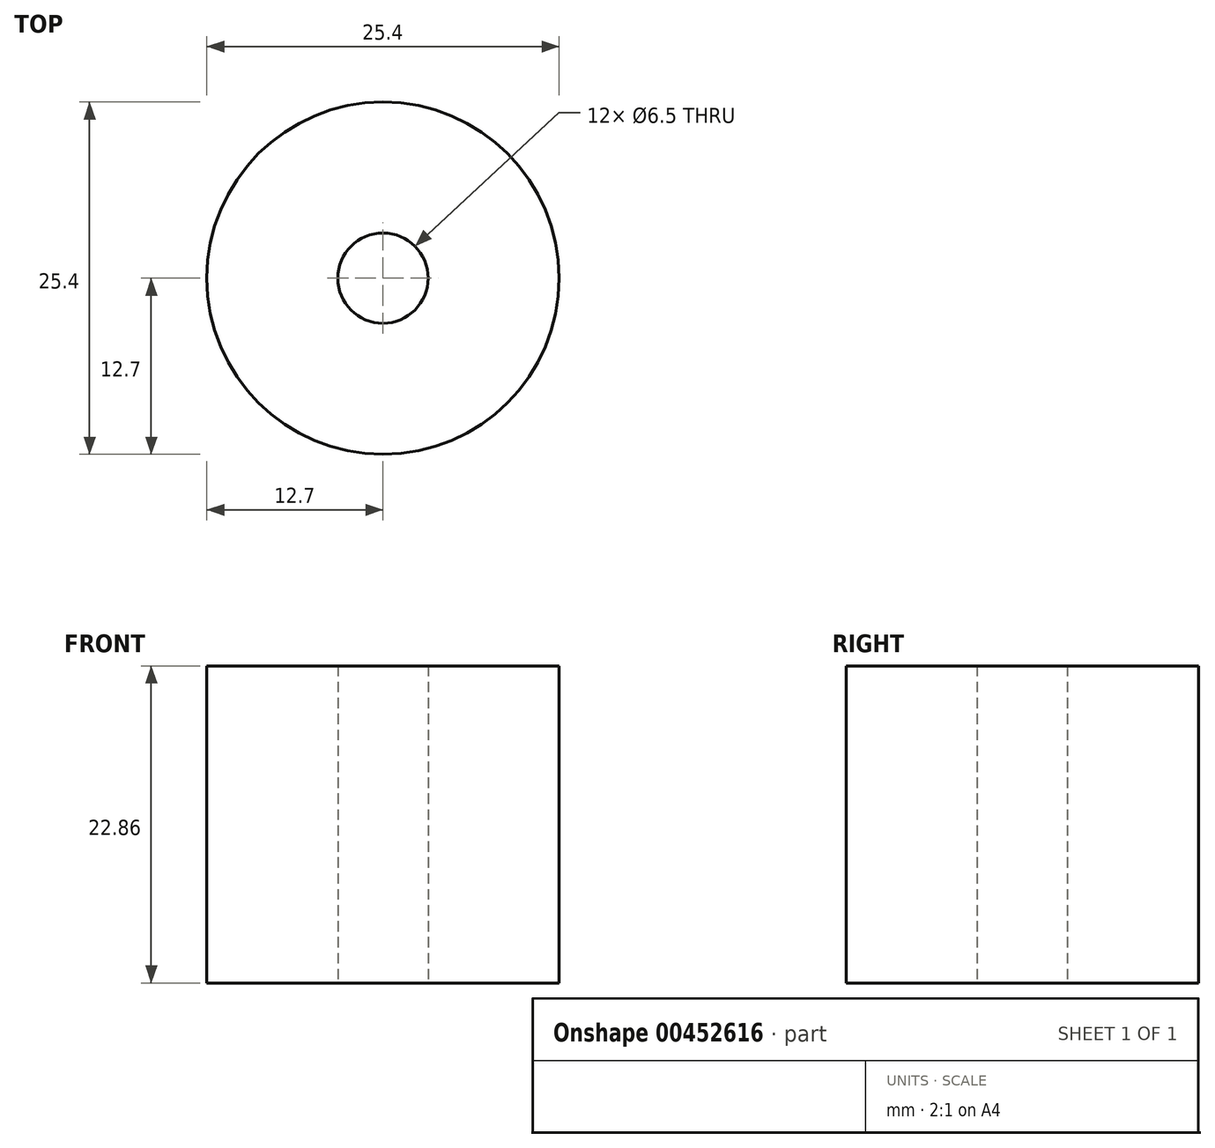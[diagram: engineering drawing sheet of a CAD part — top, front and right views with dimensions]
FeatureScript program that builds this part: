
annotation { "Feature Type Name" : "Feature", "Feature Type Description" : "" }
export const myFeature = defineFeature(function(context is Context, id is Id, definition is map)
    precondition{}
    {
        {
            var Q0;
            Q0=qCreatedBy(makeId("Top.planeOp"),FACE);
            var sketch = newSketch(context, id + "F0", { "sketchPlane" : qUnion([Q0])});
            skCircle(sketch, "E0", {"center": v(0, 0) * mm, "radius": 12.7 * mm});
            skCircle(sketch, "E1", {"center": v(0, 0) * mm, "radius": 3.25 * mm});
            skSolve(sketch);
        }
        {
            var Q0;
            Q0=makeQuery(id+"F0.imprint","IMPRINT",FACE,{"disambiguationData":[TD([[makeQuery(id+"F0.imprint","IMPRINT",EDGE,{"derivedFrom":sQuery(id+"F0.wireOp",EDGE,"E0")}),1.0]])]});
            extrude(context, id + "F1", {"entities" : qUnion([Q0]), "depth" : 22.86 * mm, "offsetDistance" : 25.4 * mm});
        }
    });
